# Revit family: Wall_Box_And_Flush_Valve-Recessed-Acorn_Dura-Ware-2803-1_Series
name_source: partatom
category: Plumbing Fixtures
units: mm (PartAtom-declared; Revit-internal decimal feet)

## family parameters
Cut with Voids When Loaded = No
Host = Face
OmniClass Number = 23.65.70.00
OmniClass Title = Terminals for Supplied Liquids and Gases
Part Type = Normal
Room Calculation Point = No
Round Connector Dimension = Use Diameter
Shared = Yes

## types (2) — shared parameters
-EG Enviro-Glaze, Specify Color = No
-EVSFV Master-Trol Electronic Flush Valve = No
-EVSPFV Master-Trol Electronic Flush Valve w/Piezo Button = No
-FV Flush Valve (Pushbutton Centered Only) = No
-FVH Hydraulic Flush Valve = No
-MTPFV Master-Trol PLUS Electronic Flush Valve = No
-MTPPFV Master-Trol PLUS Electronic Flush Valve w/Piezo Button = No
-MVCFV Time-Trol Electronic Flush Valve = No
-PBH Hemispherical Pushbutton (Electronic Valves Only) = No
-TF Transformer, 120VAC to 24VAC = No
ADA Compliant = Yes
Assembly Code = D2020300
CW Connection = Yes
CWFU = 5
Default Elevation = 0"
Description = Recessed Wall Box and Flush Valve for Remote Mounting
Door Visibility = Yes
Flush Valve Material = Metal-Acorn-Cast Bronze
HW Connection = No
Height = 14"
Inlet Connection Diameter = 1"
Installation Instruction Link = https://www.acorneng.com
Installation Type = Recessed Wall Mounted
Length = 14"
Manufacturer = Acorn Engineering
Material = Stainless Steel-Acorn Engineering-Satin
Outlet Diameter = 1"
Product Documentation Link = https://www.acorneng.com
Product Page URL = https://www.acorneng.com
TOILET FLUSH VALVE PUSHBUTTON LOCATION-LH Left Hand = No
TOILET FLUSH VALVE PUSHBUTTON LOCATION-RH Right Hand = No
TOILET FLUSH VALVE-1.28 GPF (HET) = No
TOILET FLUSH VALVE-1.6 GPF (Not Available in California) = No
TOILET FLUSH VALVE-3.5 GPF (Not Available in California) = No
URL = https://www.acorneng.com
Vent Connection = No
WFU = 5
Wall Box Material = Stainless Steel-Acorn Engineering-Satin
Wall Opening Width and Height = 13"
Waste Connection = No
Width = 4 1/2"
zero-valued in all types: HWFU

## per-type parameters (varying)
| type | Dimension A |
| 2803-1-(Standard Flush Valve) | 4 1/8" |
| 2803-1-(Hydraulic Flush Valve) | 6 1/2" |

note: column(s) folded — value = type name in every type: Model

## geometry (parser evidence)
native form markers: Sweep x4
no freeform markers — native parametric forms only
